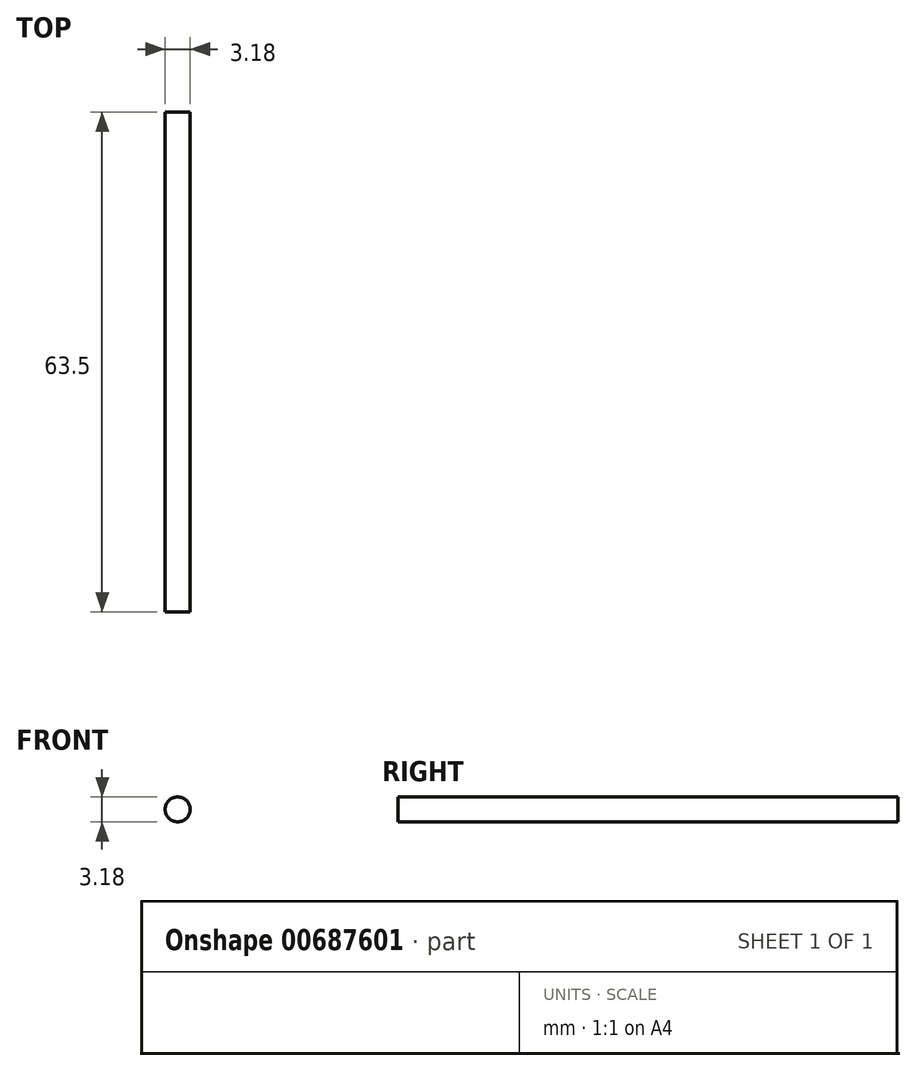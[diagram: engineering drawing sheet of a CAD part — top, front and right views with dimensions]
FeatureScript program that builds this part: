
annotation { "Feature Type Name" : "Feature", "Feature Type Description" : "" }
export const myFeature = defineFeature(function(context is Context, id is Id, definition is map)
    precondition{}
    {
        {
            var Q0;
            Q0=qCreatedBy(makeId("Front.planeOp"),FACE);
            var sketch = newSketch(context, id + "F0", { "sketchPlane" : qUnion([Q0])});
            skCircle(sketch, "E0", {"center": v(0, 0) * mm, "radius": 1.59 * mm});
            skSolve(sketch);
        }
        {
            var Q0;
            Q0=makeQuery(id+"F0.imprint","IMPRINT",FACE,{"disambiguationData":[TD([[makeQuery(id+"F0.imprint","IMPRINT",EDGE,{"derivedFrom":sQuery(id+"F0.wireOp",EDGE,"E0")}),1.0]])]});
            var Q1;
            Q1=sQuery(id+"F0.wireOp",EDGE,"E0");
            extrude(context, id + "F1", {"entities" : qUnion([Q0]), "surfaceEntities" : qUnion([Q1]), "depth" : 63.5 * mm, "offsetDistance" : 25.4 * mm});
        }
    });
